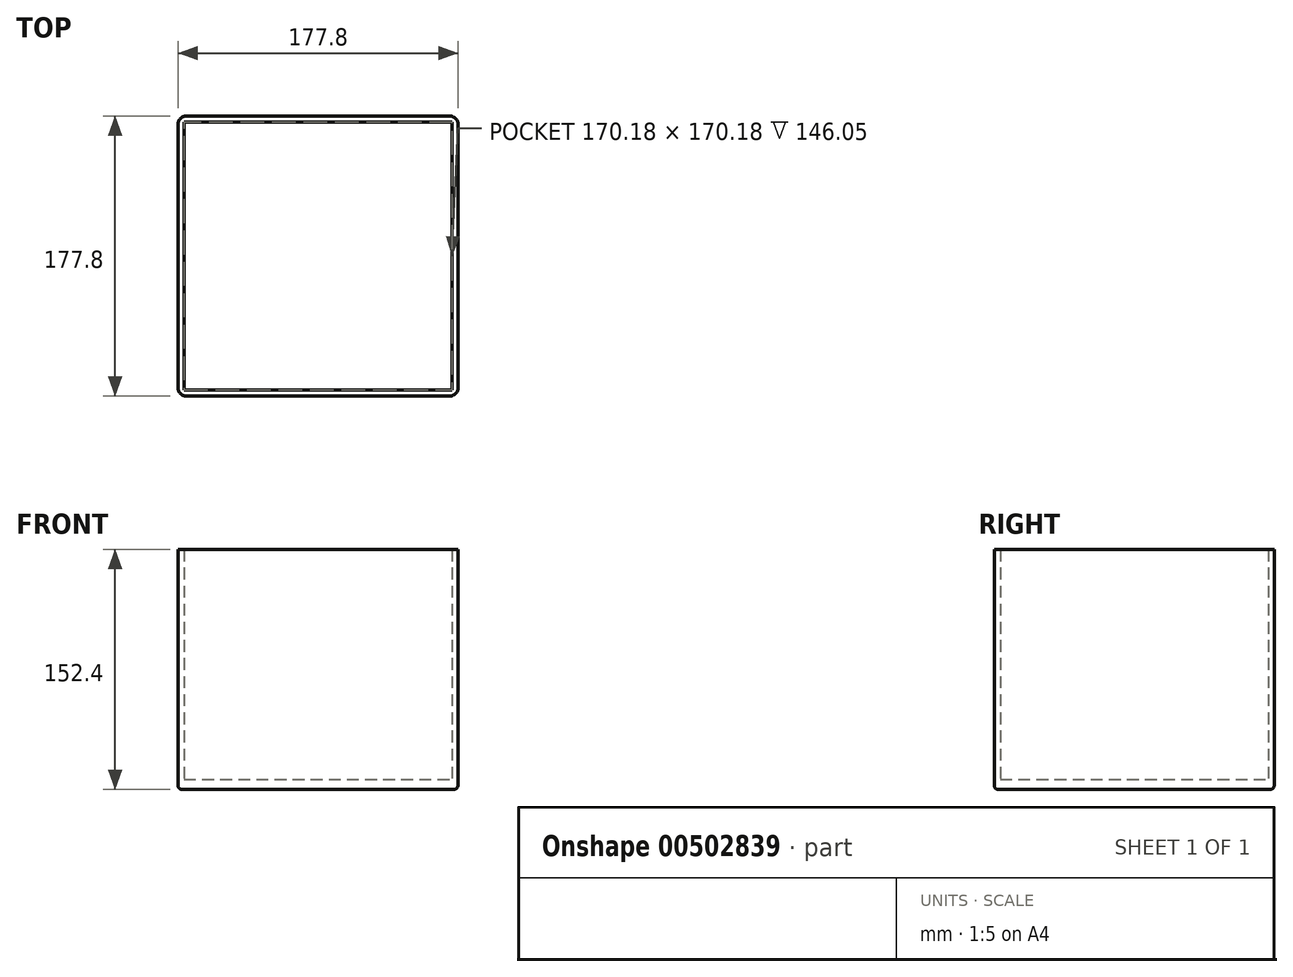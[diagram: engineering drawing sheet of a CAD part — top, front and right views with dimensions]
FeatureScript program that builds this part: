
annotation { "Feature Type Name" : "Feature", "Feature Type Description" : "" }
export const myFeature = defineFeature(function(context is Context, id is Id, definition is map)
    precondition{}
    {
        {
            var Q0;
            Q0=qCreatedBy(makeId("Top.planeOp"),FACE);
            var sketch = newSketch(context, id + "F0", { "sketchPlane" : qUnion([Q0])});
            skLineSegment(sketch, "E0.bottom", {"start": v(88.9, 88.9) * mm, "end": v(-88.9, 88.9) * mm});
            skLineSegment(sketch, "E0.top", {"start": v(88.9, -88.9) * mm, "end": v(-88.9, -88.9) * mm});
            skLineSegment(sketch, "E0.left", {"start": v(88.9, 88.9) * mm, "end": v(88.9, -88.9) * mm});
            skLineSegment(sketch, "E0.right", {"start": v(-88.9, 88.9) * mm, "end": v(-88.9, -88.9) * mm});
            skPoint(sketch, "E0.middle", {"position": v(0, 0) * mm});
            skLineSegment(sketch, "E1.bottom", {"start": v(-85.1, -85.1) * mm, "end": v(85.1, -85.1) * mm});
            skLineSegment(sketch, "E1.top", {"start": v(-85.1, 85.1) * mm, "end": v(85.1, 85.1) * mm});
            skLineSegment(sketch, "E1.left", {"start": v(-85.1, -85.1) * mm, "end": v(-85.1, 85.1) * mm});
            skLineSegment(sketch, "E1.right", {"start": v(85.1, -85.1) * mm, "end": v(85.1, 85.1) * mm});
            skLineSegment(sketch, "E2", {"start": v(0, 0) * mm, "end": v(-88.9, 0) * mm});
            skLineSegment(sketch, "E3", {"start": v(0, 0) * mm, "end": v(0, 88.9) * mm});
            skLineSegment(sketch, "E4", {"start": v(0, 0) * mm, "end": v(88.9, 0) * mm});
            skLineSegment(sketch, "E5", {"start": v(0, 0) * mm, "end": v(0, -88.9) * mm});
            skLineSegment(sketch, "E6", {"start": v(0, 44.45) * mm, "end": v(-10.16, 44.45) * mm});
            skPoint(sketch, "E6.endSnap0", {"position": v(0, 44.45) * mm});
            skLineSegment(sketch, "E7", {"start": v(-44.45, 0) * mm, "end": v(-44.45, -10.16) * mm});
            skLineSegment(sketch, "E8", {"start": v(44.45, 0) * mm, "end": v(44.45, 10.16) * mm});
            skLineSegment(sketch, "E9", {"start": v(0, -44.45) * mm, "end": v(10.16, -44.45) * mm});
            skLineSegment(sketch, "E10", {"start": v(10.16, -44.45) * mm, "end": v(10.16, -62.23) * mm});
            skLineSegment(sketch, "E11", {"start": v(10.16, -44.45) * mm, "end": v(10.16, -26.67) * mm});
            skLineSegment(sketch, "E12", {"start": v(44.45, 10.16) * mm, "end": v(62.23, 10.16) * mm});
            skLineSegment(sketch, "E13", {"start": v(44.45, 10.16) * mm, "end": v(26.67, 10.16) * mm});
            skLineSegment(sketch, "E14", {"start": v(-44.45, -10.16) * mm, "end": v(-62.23, -10.16) * mm});
            skLineSegment(sketch, "E15", {"start": v(-44.45, -10.16) * mm, "end": v(-26.67, -10.16) * mm});
            skLineSegment(sketch, "E16", {"start": v(-10.16, 44.45) * mm, "end": v(-10.16, 26.67) * mm});
            skLineSegment(sketch, "E17", {"start": v(-10.16, 44.45) * mm, "end": v(-10.16, 62.23) * mm});
            skLineSegment(sketch, "E18", {"start": v(0, 44.45) * mm, "end": v(0, 57.15) * mm});
            skLineSegment(sketch, "E19", {"start": v(0, 44.45) * mm, "end": v(0, 31.75) * mm});
            skLineSegment(sketch, "E20", {"start": v(-44.45, 0) * mm, "end": v(-57.15, 0) * mm});
            skLineSegment(sketch, "E21", {"start": v(-44.45, 0) * mm, "end": v(-31.75, 0) * mm});
            skLineSegment(sketch, "E22.MirrorCS", {"start": v(0, -44.45) * mm, "end": v(0, -57.15) * mm});
            skPoint(sketch, "E23.MirrorP", {"position": v(0, -44.45) * mm});
            skLineSegment(sketch, "E24.MirrorCS", {"start": v(0, -44.45) * mm, "end": v(0, -31.75) * mm});
            skLineSegment(sketch, "E25.MirrorCS", {"start": v(0, -44.45) * mm, "end": v(-10.16, -44.45) * mm});
            skLineSegment(sketch, "E26.MirrorCS", {"start": v(44.45, 0) * mm, "end": v(44.45, -10.16) * mm});
            skLineSegment(sketch, "E27.MirrorCS", {"start": v(44.45, 0) * mm, "end": v(57.15, 0) * mm});
            skLineSegment(sketch, "E28.MirrorCS", {"start": v(44.45, 0) * mm, "end": v(31.75, 0) * mm});
            skLineSegment(sketch, "E29", {"start": v(26.67, 10.16) * mm, "end": v(31.75, 0) * mm});
            skLineSegment(sketch, "E30", {"start": v(62.23, 10.16) * mm, "end": v(57.15, 0) * mm});
            skLineSegment(sketch, "E31", {"start": v(10.16, -26.67) * mm, "end": v(0, -31.75) * mm});
            skLineSegment(sketch, "E32", {"start": v(10.16, -62.23) * mm, "end": v(0, -57.15) * mm});
            skLineSegment(sketch, "E33", {"start": v(-31.75, 0) * mm, "end": v(-26.67, -10.16) * mm});
            skLineSegment(sketch, "E34", {"start": v(-57.15, 0) * mm, "end": v(-62.23, -10.16) * mm});
            skLineSegment(sketch, "E35", {"start": v(0, 57.15) * mm, "end": v(-10.16, 62.23) * mm});
            skLineSegment(sketch, "E36", {"start": v(0, 31.75) * mm, "end": v(-10.16, 26.67) * mm});
            skSolve(sketch);
        }
        {
            var Q0;
            Q0=makeQuery(id+"F0.imprint","IMPRINT",FACE,{"disambiguationData":[TD([[makeQuery(id+"F0.imprint","IMPRINT",EDGE,{"derivedFrom":sQuery(id+"F0.wireOp",EDGE,"E0.bottom")}),1.0]])]});
            var Q1;
            {var subQ5=sQuery(id+"F0.wireOp",EDGE,"E0.right");var subQ6=sQuery(id+"F0.wireOp",EDGE,"E0.top");var subQ7=makeQuery(id+"F0.imprint","INTERSECT",VERTEX,{"derivedFrom":[subQ6,subQ5]});Q1=makeQuery(id+"F0.imprint","IMPRINT",FACE,{"disambiguationData":[TD([[makeQuery(id+"F0.imprint","IMPRINT",EDGE,{"disambiguationData":[TD([[subQ7,1.0]])],"derivedFrom":subQ6}),-1.0]])]});}
            var Q2;
            {var subQ5=sQuery(id+"F0.wireOp",EDGE,"E0.left");var subQ9=sQuery(id+"F0.wireOp",EDGE,"E0.top");var subQ10=makeQuery(id+"F0.imprint","INTERSECT",VERTEX,{"derivedFrom":[subQ9,subQ5]});Q2=makeQuery(id+"F0.imprint","IMPRINT",FACE,{"disambiguationData":[TD([[makeQuery(id+"F0.imprint","IMPRINT",EDGE,{"disambiguationData":[TD([[subQ10,-1.0]])],"derivedFrom":subQ9}),-1.0]])]});}
            extrude(context, id + "F1", {"entities" : qUnion([Q0, Q1, Q2]), "depth" : 152.4 * mm});
        }
        {
            var Q0;
            Q0=makeQuery(id+"F0.imprint","IMPRINT",FACE,{"disambiguationData":[TD([[makeQuery(id+"F0.imprint","IMPRINT",EDGE,{"derivedFrom":sQuery(id+"F0.wireOp",EDGE,"E10")}),1.0]])]});
            var Q1;
            Q1=makeQuery(id+"F0.imprint","IMPRINT",FACE,{"disambiguationData":[TD([[makeQuery(id+"F0.imprint","IMPRINT",EDGE,{"derivedFrom":sQuery(id+"F0.wireOp",EDGE,"E16")}),-1.0]])]});
            var Q2;
            {var subQ0=sQuery(id+"F0.wireOp",EDGE,"E8");Q2=makeQuery(id+"F0.imprint","IMPRINT",FACE,{"disambiguationData":[TD([[makeQuery(id+"F0.imprint","IMPRINT",EDGE,{"derivedFrom":subQ0}),-1.0]])]});}
            var Q3;
            {var subQ0=sQuery(id+"F0.wireOp",EDGE,"E8");Q3=makeQuery(id+"F0.imprint","IMPRINT",FACE,{"disambiguationData":[TD([[makeQuery(id+"F0.imprint","IMPRINT",EDGE,{"derivedFrom":subQ0}),1.0]])]});}
            var Q4;
            Q4=makeQuery(id+"F0.imprint","IMPRINT",FACE,{"disambiguationData":[TD([[makeQuery(id+"F0.imprint","IMPRINT",EDGE,{"derivedFrom":sQuery(id+"F0.wireOp",EDGE,"E6")}),1.0]])]});
            var Q5;
            Q5=makeQuery(id+"F0.imprint","IMPRINT",FACE,{"disambiguationData":[TD([[makeQuery(id+"F0.imprint","IMPRINT",EDGE,{"derivedFrom":sQuery(id+"F0.wireOp",EDGE,"E6")}),-1.0]])]});
            var Q6;
            Q6=makeQuery(id+"F0.imprint","IMPRINT",FACE,{"disambiguationData":[TD([[makeQuery(id+"F0.imprint","IMPRINT",EDGE,{"derivedFrom":sQuery(id+"F0.wireOp",EDGE,"E12")}),1.0]])]});
            var Q7;
            Q7=makeQuery(id+"F0.imprint","IMPRINT",FACE,{"disambiguationData":[TD([[makeQuery(id+"F0.imprint","IMPRINT",EDGE,{"derivedFrom":sQuery(id+"F0.wireOp",EDGE,"E14")}),1.0]])]});
            var Q8;
            Q8=makeQuery(id+"F0.imprint","IMPRINT",FACE,{"disambiguationData":[TD([[makeQuery(id+"F0.imprint","IMPRINT",EDGE,{"derivedFrom":sQuery(id+"F0.wireOp",EDGE,"E9")}),1.0]])]});
            var Q9;
            {var subQ0=sQuery(id+"F0.wireOp",EDGE,"E9");Q9=makeQuery(id+"F0.imprint","IMPRINT",FACE,{"disambiguationData":[TD([[makeQuery(id+"F0.imprint","IMPRINT",EDGE,{"derivedFrom":subQ0}),-1.0]])]});}
            var Q10;
            Q10=makeQuery(id+"F0.imprint","IMPRINT",FACE,{"disambiguationData":[TD([[makeQuery(id+"F0.imprint","IMPRINT",EDGE,{"derivedFrom":sQuery(id+"F0.wireOp",EDGE,"E7")}),1.0]])]});
            var Q11;
            Q11=makeQuery(id+"F0.imprint","IMPRINT",FACE,{"disambiguationData":[TD([[makeQuery(id+"F0.imprint","IMPRINT",EDGE,{"derivedFrom":sQuery(id+"F0.wireOp",EDGE,"E7")}),-1.0]])]});
            extrude(context, id + "F2", {"entities" : qUnion([Q0, Q1, Q2, Q3, Q4, Q5, Q6, Q7, Q8, Q9, Q10, Q11]), "operationType" : NewBodyOperationType.ADD, "depth" : 6.35 * mm});
        }
        {
            var Q0;
            Q0=makeQuery(id+"F1.opExtrude","SWEPT_FACE",FACE,{"disambiguationData":[OSD([sQuery(id+"F0.wireOp",EDGE,"E0.top")])]});
            var sketch = newSketch(context, id + "F3", { "sketchPlane" : qUnion([Q0])});
            skPoint(sketch, "E37", {"position": v(0, 152.4) * mm});
            skLineSegment(sketch, "E38", {"start": v(0, 152.4) * mm, "end": v(-50.8, 152.4) * mm});
            skLineSegment(sketch, "E39", {"start": v(0, 152.4) * mm, "end": v(50.8, 152.4) * mm});
            skLineSegment(sketch, "E40", {"start": v(0, 152.4) * mm, "end": v(0, 139.7) * mm});
            skLineSegment(sketch, "E41", {"start": v(0, 139.7) * mm, "end": v(-60.96, 139.7) * mm});
            skLineSegment(sketch, "E42", {"start": v(-60.96, 139.7) * mm, "end": v(-50.8, 152.4) * mm});
            skLineSegment(sketch, "E43", {"start": v(0, 139.7) * mm, "end": v(60.96, 139.7) * mm});
            skLineSegment(sketch, "E44", {"start": v(60.96, 139.7) * mm, "end": v(50.8, 152.4) * mm});
            skSolve(sketch);
        }
        {
            var Q0;
            Q0=makeQuery(id+"F1.opExtrude","SWEPT_EDGE",EDGE,{"disambiguationData":[OSD([sQuery(id+"F0.wireOp",EDGE,"E0.bottom"),sQuery(id+"F0.wireOp",EDGE,"E0.right")])]});
            var Q1;
            Q1=makeQuery(id+"F1.opExtrude","SWEPT_EDGE",EDGE,{"disambiguationData":[OSD([sQuery(id+"F0.wireOp",EDGE,"E0.bottom"),sQuery(id+"F0.wireOp",EDGE,"E0.left")])]});
            var Q2;
            Q2=makeQuery(id+"F1.opExtrude","SWEPT_EDGE",EDGE,{"disambiguationData":[OSD([sQuery(id+"F0.wireOp",EDGE,"E0.top"),sQuery(id+"F0.wireOp",EDGE,"E0.left")])]});
            var Q3;
            Q3=makeQuery(id+"F1.opExtrude","SWEPT_EDGE",EDGE,{"disambiguationData":[OSD([sQuery(id+"F0.wireOp",EDGE,"E0.top"),sQuery(id+"F0.wireOp",EDGE,"E0.right")])]});
            fillet(context, id + "F4", {"entities" : qUnion([Q0, Q1, Q2, Q3]), "radius" : 5.08 * mm, "tangentPropagation" : true, "allowEdgeOverflow" : false});
        }
        {
            var Q0;
            {var subQ0=sQuery(id+"F0.wireOp",EDGE,"E1.right");var subQ1=sQuery(id+"F0.wireOp",EDGE,"E1.left");var subQ2=sQuery(id+"F0.wireOp",EDGE,"E1.top");var subQ3=sQuery(id+"F0.wireOp",EDGE,"E1.bottom");Q0=makeQuery(id+"F2.boolean.opBoolean","MERGE",FACE,{"derivedFrom":[makeQuery(id+"F1.opExtrude","CAP_FACE",FACE,{"disambiguationData":[OSD([sQuery(id+"F0.wireOp",EDGE,"E0.bottom"),sQuery(id+"F0.wireOp",EDGE,"E0.top"),sQuery(id+"F0.wireOp",EDGE,"E0.left"),sQuery(id+"F0.wireOp",EDGE,"E0.right"),subQ3,subQ2,subQ1,subQ0])],"isStart":true}),makeQuery(id+"F2.opExtrude","CAP_FACE",FACE,{"disambiguationData":[OSD([subQ3,subQ2,subQ1,subQ0])],"isStart":true})]});}
            fillet(context, id + "F5", {"entities" : qUnion([Q0]), "radius" : 2.54 * mm, "tangentPropagation" : true, "allowEdgeOverflow" : false});
        }
    });
